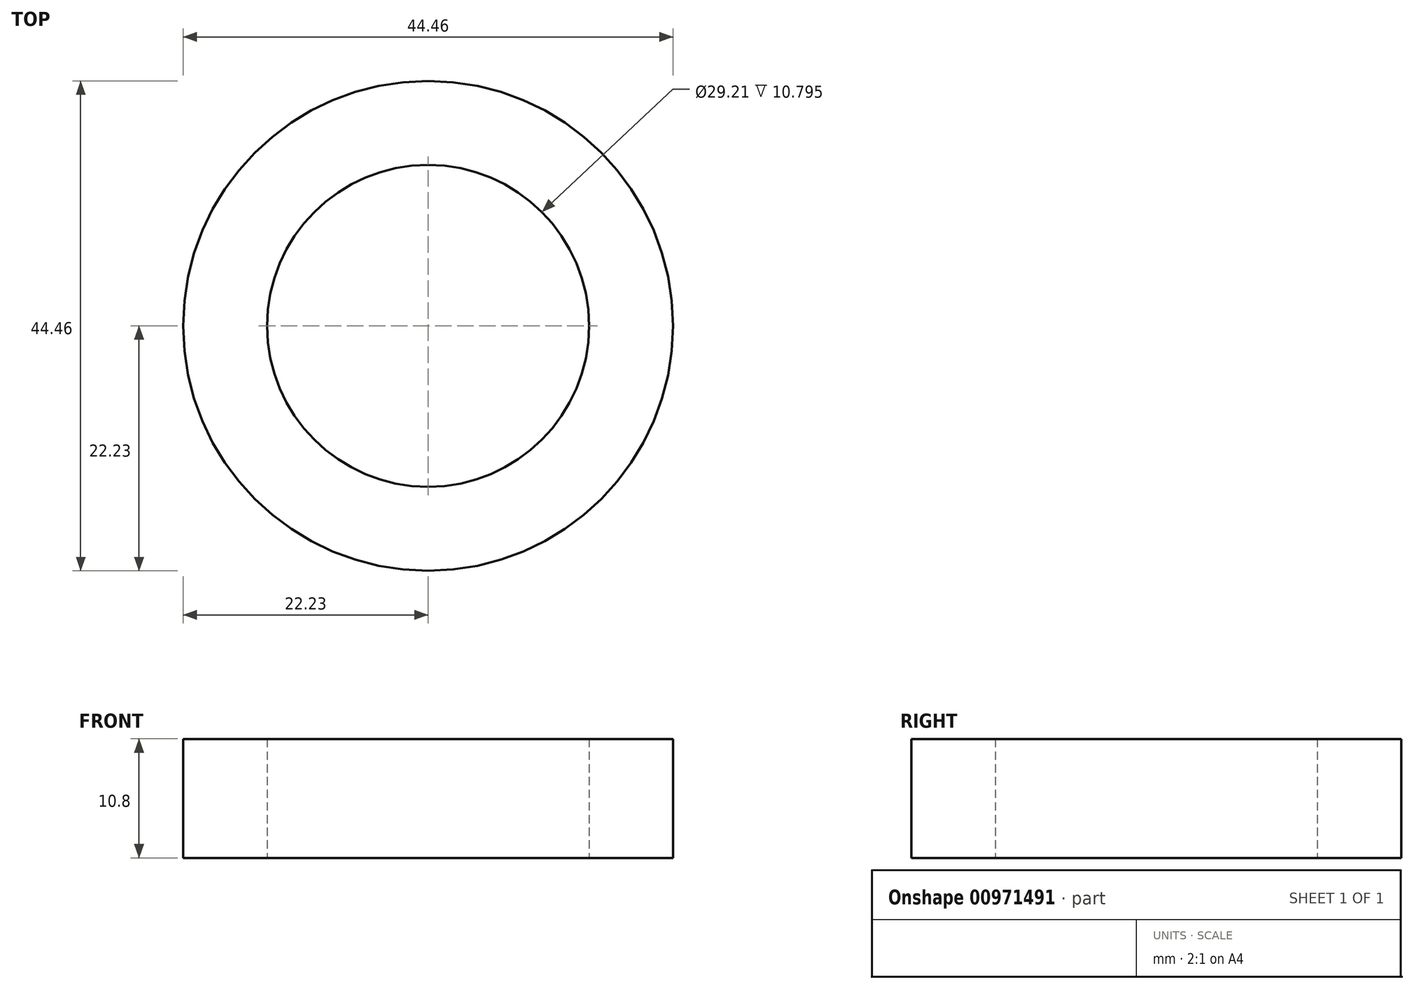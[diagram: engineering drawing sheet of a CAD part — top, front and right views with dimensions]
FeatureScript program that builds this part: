
annotation { "Feature Type Name" : "Feature", "Feature Type Description" : "" }
export const myFeature = defineFeature(function(context is Context, id is Id, definition is map)
    precondition{}
    {
        {
            var Q0;
            Q0=qCreatedBy(makeId("Top.planeOp"),FACE);
            var sketch = newSketch(context, id + "F0", { "sketchPlane" : qUnion([Q0])});
            skCircle(sketch, "E0", {"center": v(0, 0) * mm, "radius": 9.53 * mm});
            skCircle(sketch, "E1", {"center": v(0, 0) * mm, "radius": 14.6 * mm});
            skCircle(sketch, "E2", {"center": v(0, 0) * mm, "radius": 22.23 * mm});
            skSolve(sketch);
        }
        {
            var Q0;
            Q0=makeQuery(id+"F0.imprint","IMPRINT",FACE,{"disambiguationData":[TD([[makeQuery(id+"F0.imprint","IMPRINT",EDGE,{"derivedFrom":sQuery(id+"F0.wireOp",EDGE,"E1")}),-1.0]])]});
            extrude(context, id + "F1", {"entities" : qUnion([Q0]), "depth" : 10.8 * mm, "offsetDistance" : 25.4 * mm});
        }
    });
